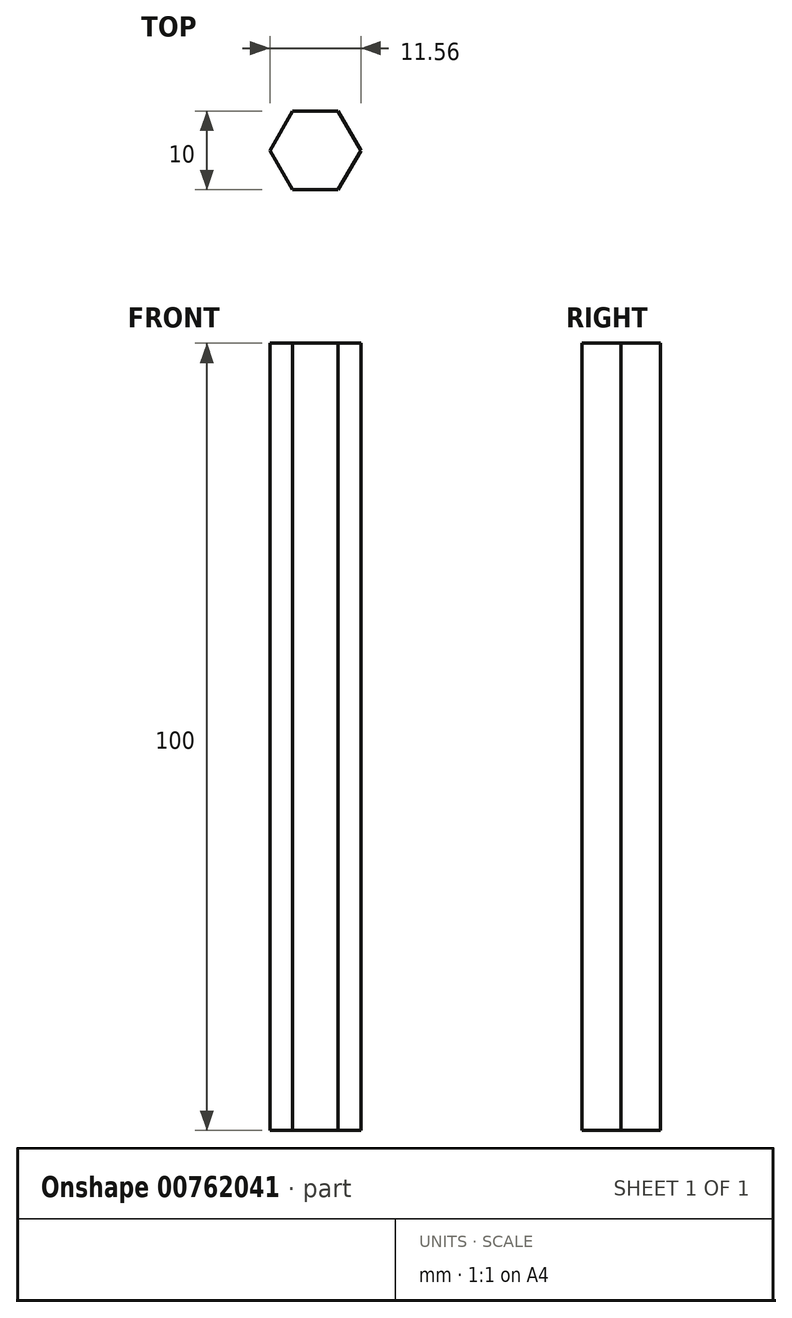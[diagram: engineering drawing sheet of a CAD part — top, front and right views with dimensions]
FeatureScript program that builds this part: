
annotation { "Feature Type Name" : "Feature", "Feature Type Description" : "" }
export const myFeature = defineFeature(function(context is Context, id is Id, definition is map)
    precondition{}
    {
        {
            var Q0;
            Q0=qCreatedBy(makeId("Top.planeOp"),FACE);
            var sketch = newSketch(context, id + "F0", { "sketchPlane" : qUnion([Q0])});
            skCircle(sketch, "E0.cCircle", {"center": v(0, 0) * mm, "radius": 5 * mm, "construction": true});
            skLineSegment(sketch, "E0.0", {"start": v(2.89, 5) * mm, "end": v(5.78, 0) * mm});
            skLineSegment(sketch, "E0.1", {"start": v(5.78, 0) * mm, "end": v(2.89, -5) * mm});
            skLineSegment(sketch, "E0.2", {"start": v(2.89, -5) * mm, "end": v(-2.89, -5) * mm});
            skLineSegment(sketch, "E0.3", {"start": v(-2.89, -5) * mm, "end": v(-5.78, 0) * mm});
            skLineSegment(sketch, "E0.4", {"start": v(-5.78, 0) * mm, "end": v(-2.89, 5) * mm});
            skLineSegment(sketch, "E0.5", {"start": v(-2.89, 5) * mm, "end": v(2.89, 5) * mm});
            skPoint(sketch, "E0.0.midPoint", {"position": v(4.33, 2.5) * mm});
            skSolve(sketch);
        }
        {
            var Q0;
            Q0=makeQuery(id+"F0.imprint","IMPRINT",FACE,{"disambiguationData":[TD([[makeQuery(id+"F0.imprint","IMPRINT",EDGE,{"derivedFrom":sQuery(id+"F0.wireOp",EDGE,"E0.0")}),-1.0]])]});
            extrude(context, id + "F1", {"entities" : qUnion([Q0]), "depth" : 100 * mm, "offsetDistance" : 25 * mm});
        }
    });
